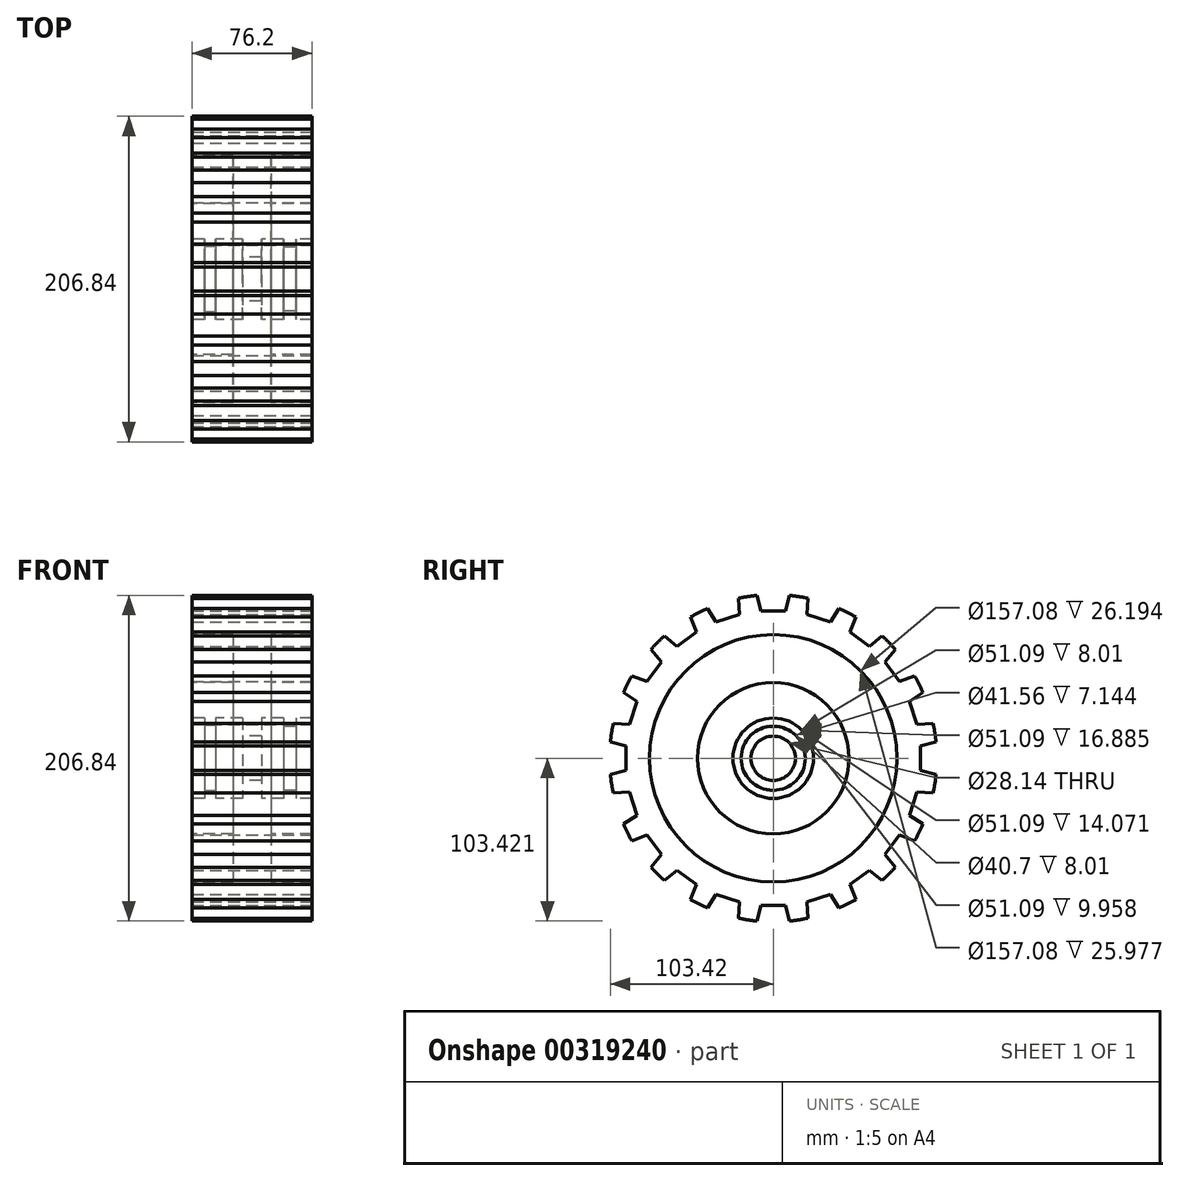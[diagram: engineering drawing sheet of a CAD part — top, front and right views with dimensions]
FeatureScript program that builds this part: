
annotation { "Feature Type Name" : "Feature", "Feature Type Description" : "" }
export const myFeature = defineFeature(function(context is Context, id is Id, definition is map)
    precondition{}
    {
        {
            var Q0;
            Q0=qCreatedBy(makeId("Front.planeOp"),FACE);
            var sketch = newSketch(context, id + "F0", { "sketchPlane" : qUnion([Q0])});
            skLineSegment(sketch, "E0.bottom", {"start": v(38.1, 61.5) * mm, "end": v(-38.1, 61.5) * mm});
            skLineSegment(sketch, "E0.top", {"start": v(38.1, 36.1) * mm, "end": v(12.12, 36.1) * mm});
            skLineSegment(sketch, "E0.left", {"start": v(38.1, 61.5) * mm, "end": v(38.1, 36.1) * mm});
            skLineSegment(sketch, "E0.right", {"start": v(-38.1, 61.5) * mm, "end": v(-38.1, 36.1) * mm});
            skPoint(sketch, "E0.middle", {"position": v(0, 48.8) * mm});
            skLineSegment(sketch, "E1.bottom", {"start": v(38.1, 5.63) * mm, "end": v(12.12, 5.63) * mm});
            skLineSegment(sketch, "E1.top", {"start": v(38.1, -16.89) * mm, "end": v(28.14, -16.89) * mm});
            skLineSegment(sketch, "E1.left", {"start": v(38.1, 5.63) * mm, "end": v(38.1, -16.89) * mm});
            skLineSegment(sketch, "E1.right", {"start": v(-38.1, 5.63) * mm, "end": v(-38.1, -16.89) * mm});
            skPoint(sketch, "E1.middle", {"position": v(0, -5.63) * mm});
            skLineSegment(sketch, "E2", {"start": v(-11.9, 36.1) * mm, "end": v(-11.9, 5.63) * mm});
            skLineSegment(sketch, "E3", {"start": v(12.12, 36.1) * mm, "end": v(12.12, 5.63) * mm});
            skLineSegment(sketch, "E4.trimOffspring", {"start": v(-11.9, 36.1) * mm, "end": v(-38.1, 36.1) * mm});
            skLineSegment(sketch, "E5.trimOffspring", {"start": v(-11.9, 5.63) * mm, "end": v(-38.1, 5.63) * mm});
            skLineSegment(sketch, "E6.top", {"start": v(-30.1, -21.65) * mm, "end": v(-22.95, -21.65) * mm});
            skLineSegment(sketch, "E6.left", {"start": v(-30.1, -16.89) * mm, "end": v(-30.1, -21.65) * mm});
            skLineSegment(sketch, "E6.right", {"start": v(-22.95, -16.89) * mm, "end": v(-22.95, -21.65) * mm});
            skLineSegment(sketch, "E7.top", {"start": v(-6.06, -28.36) * mm, "end": v(6.06, -28.36) * mm});
            skLineSegment(sketch, "E7.left", {"start": v(-6.06, -16.89) * mm, "end": v(-6.06, -28.36) * mm});
            skLineSegment(sketch, "E7.right", {"start": v(6.06, -16.89) * mm, "end": v(6.06, -28.36) * mm});
            skLineSegment(sketch, "E8.top", {"start": v(20.13, -22.08) * mm, "end": v(28.14, -22.08) * mm});
            skLineSegment(sketch, "E8.left", {"start": v(20.13, -16.89) * mm, "end": v(20.13, -22.08) * mm});
            skLineSegment(sketch, "E8.right", {"start": v(28.14, -16.89) * mm, "end": v(28.14, -22.08) * mm});
            skLineSegment(sketch, "E9.trimOffspring", {"start": v(-6.06, -16.89) * mm, "end": v(-22.95, -16.89) * mm});
            skLineSegment(sketch, "E10.trimOffspring", {"start": v(-30.1, -16.89) * mm, "end": v(-38.1, -16.89) * mm});
            skLineSegment(sketch, "E11.trimOffspring", {"start": v(20.13, -16.89) * mm, "end": v(6.06, -16.89) * mm});
            skLineSegment(sketch, "E12", {"start": v(-12.56, -42.43) * mm, "end": v(14.29, -42.43) * mm, "construction": true});
            skSolve(sketch);
        }
        {
            var Q0;
            Q0=makeQuery(id+"F0.imprint","IMPRINT",FACE,{"disambiguationData":[TD([[makeQuery(id+"F0.imprint","IMPRINT",EDGE,{"derivedFrom":sQuery(id+"F0.wireOp",EDGE,"E0.bottom")}),1.0]])]});
            var Q1;
            Q1=sQuery(id+"F0.wireOp",EDGE,"E12");
            revolve(context, id + "F1", {"entities" : qUnion([Q0]), "axis" : qUnion([Q1]), "revolveType" : RevolveType.FULL});
        }
        {
            var Q0;
            Q0=makeQuery(id+"F1.opRevolve","SWEPT_FACE",FACE,{"disambiguationData":[OSD([sQuery(id+"F0.wireOp",EDGE,"E8.right")])]});
            var sketch = newSketch(context, id + "F2", { "sketchPlane" : qUnion([Q0])});
            skLineSegment(sketch, "E13", {"start": v(-11.66, 65.87) * mm, "end": v(-7.73, 51.07) * mm});
            skLineSegment(sketch, "E14", {"start": v(-7.73, 51.07) * mm, "end": v(0, 51.07) * mm});
            skLineSegment(sketch, "E15", {"start": v(-11.66, 65.87) * mm, "end": v(0, 65.87) * mm});
            skLineSegment(sketch, "E16.MirrorCS", {"start": v(11.66, 65.87) * mm, "end": v(0, 65.87) * mm});
            skLineSegment(sketch, "E17.MirrorCS", {"start": v(11.66, 65.87) * mm, "end": v(7.73, 51.07) * mm});
            skLineSegment(sketch, "E18.MirrorCS", {"start": v(7.73, 51.07) * mm, "end": v(0, 51.07) * mm});
            skSolve(sketch);
        }
        {
            var Q0;
            Q0=makeQuery(id+"F2.imprint","IMPRINT",FACE,{"disambiguationData":[TD([[makeQuery(id+"F2.imprint","IMPRINT",EDGE,{"derivedFrom":sQuery(id+"F2.wireOp",EDGE,"E13")}),1.0]])]});
            extrude(context, id + "F3", {"entities" : qUnion([Q0]), "operationType" : NewBodyOperationType.REMOVE, "endBound" : BoundingType.SYMMETRIC, "oppositeDirection" : true, "depth" : 177.3 * mm});
        }
        {
            var Q0;
            Q0=makeQuery(id+"F3.boolean.opBoolean","COPY",FACE,{"derivedFrom":makeQuery(id+"F3.opExtrude","SWEPT_FACE",FACE,{"disambiguationData":[OSD([sQuery(id+"F2.wireOp",EDGE,"E13")])]})});
            var Q1;
            Q1=makeQuery(id+"F3.boolean.opBoolean","COPY",FACE,{"derivedFrom":makeQuery(id+"F3.opExtrude","SWEPT_FACE",FACE,{"disambiguationData":[OSD([sQuery(id+"F2.wireOp",EDGE,"E14"),sQuery(id+"F2.wireOp",EDGE,"E18.MirrorCS")])]})});
            var Q2;
            Q2=makeQuery(id+"F3.boolean.opBoolean","COPY",FACE,{"derivedFrom":makeQuery(id+"F3.opExtrude","SWEPT_FACE",FACE,{"disambiguationData":[OSD([sQuery(id+"F2.wireOp",EDGE,"E17.MirrorCS")])]})});
            var Q3;
            Q3=makeQuery(id+"F1.opRevolve","SWEPT_EDGE",EDGE,{"disambiguationData":[OSD([sQuery(id+"F0.wireOp",EDGE,"E0.top"),sQuery(id+"F0.wireOp",EDGE,"E0.left")])]});
            circularPattern(context, id + "F4", {"patternType" : PatternType.FACE, "faces" : qUnion([Q0, Q1, Q2]), "axis" : qUnion([Q3]), "angle" : 360 * degree, "instanceCount" : 40, "equalSpace" : true});
        }
    });
